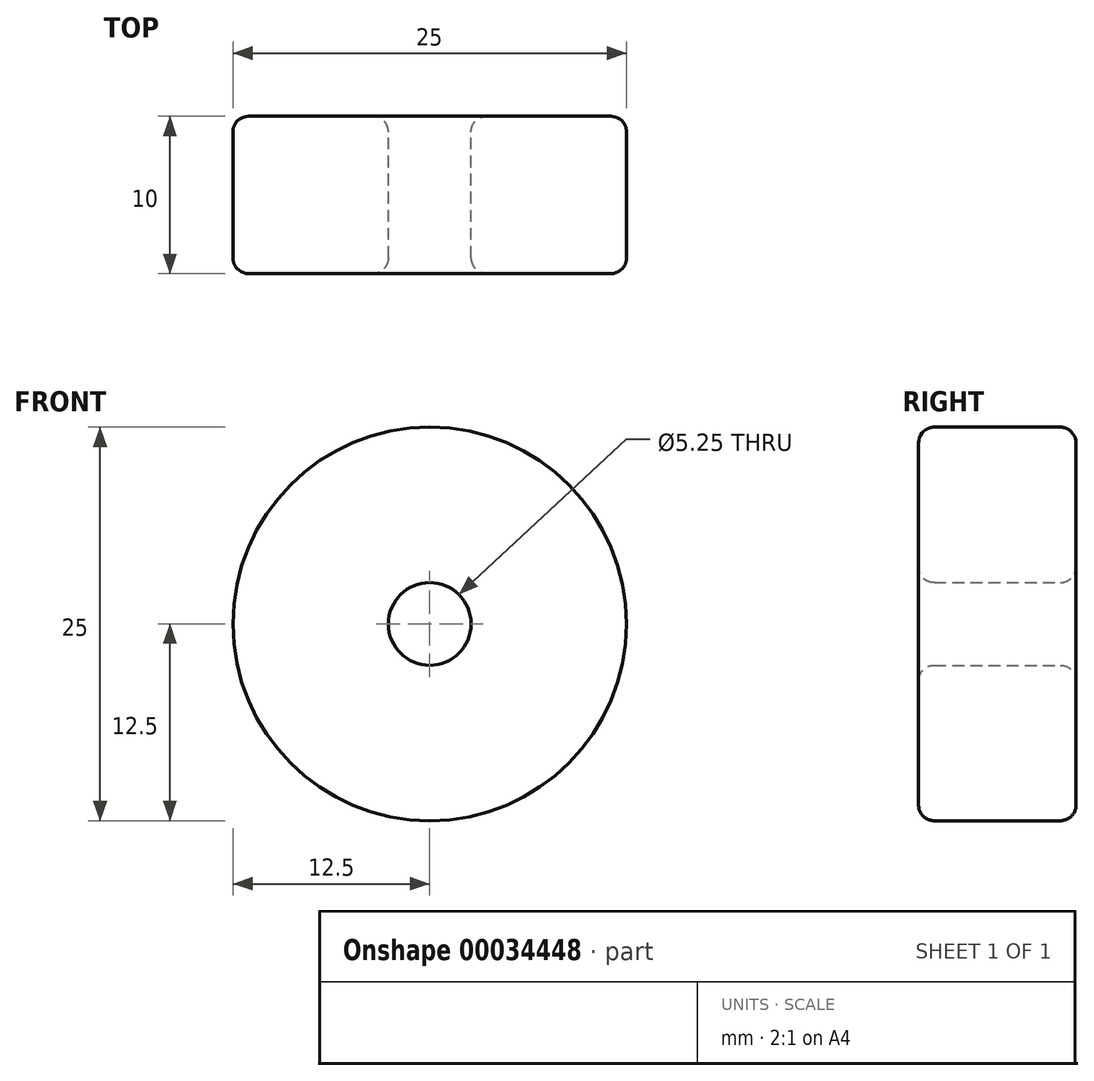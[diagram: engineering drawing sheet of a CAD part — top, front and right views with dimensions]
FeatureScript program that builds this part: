
annotation { "Feature Type Name" : "Feature", "Feature Type Description" : "" }
export const myFeature = defineFeature(function(context is Context, id is Id, definition is map)
    precondition{}
    {
        {
            var Q0;
            Q0=qCreatedBy(makeId("Front.planeOp"),FACE);
            var sketch = newSketch(context, id + "F0", { "sketchPlane" : qUnion([Q0])});
            skCircle(sketch, "E0", {"center": v(0, 0) * mm, "radius": 12.5 * mm});
            skCircle(sketch, "E1", {"center": v(0, 0) * mm, "radius": 2.63 * mm});
            skSolve(sketch);
        }
        {
            var Q0;
            Q0 = qSketchRegion(id + "F0", true);
            extrude(context, id + "F1", {"entities" : qUnion([Q0]), "depth" : 10 * mm});
        }
        {
            var Q0;
            Q0=makeQuery(id+"F1.opExtrude","CAP_EDGE",EDGE,{"disambiguationData":[OSD([sQuery(id+"F0.wireOp",EDGE,"E0")])],"isStart":false});
            var Q1;
            Q1=makeQuery(id+"F1.opExtrude","CAP_EDGE",EDGE,{"disambiguationData":[OSD([sQuery(id+"F0.wireOp",EDGE,"E0")])],"isStart":true});
            var Q2;
            Q2=makeQuery(id+"F1.opExtrude","CAP_EDGE",EDGE,{"disambiguationData":[OSD([sQuery(id+"F0.wireOp",EDGE,"E1")])],"isStart":false});
            var Q3;
            Q3=makeQuery(id+"F1.opExtrude","CAP_EDGE",EDGE,{"disambiguationData":[OSD([sQuery(id+"F0.wireOp",EDGE,"E1")])],"isStart":true});
            fillet(context, id + "F2", {"entities" : qUnion([Q0, Q1, Q2, Q3]), "radius" : 1 * mm, "tangentPropagation" : true, "allowEdgeOverflow" : false});
        }
    });
